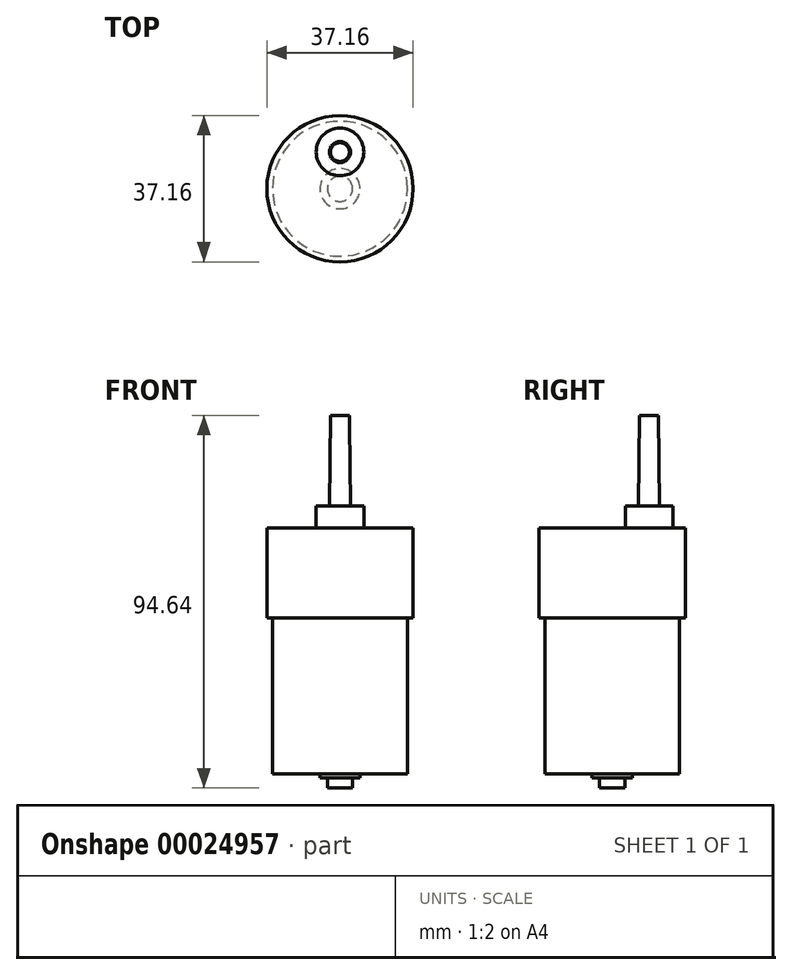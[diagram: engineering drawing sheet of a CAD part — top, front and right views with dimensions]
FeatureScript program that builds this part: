
annotation { "Feature Type Name" : "Feature", "Feature Type Description" : "" }
export const myFeature = defineFeature(function(context is Context, id is Id, definition is map)
    precondition{}
    {
        {
            var Q0;
            Q0=qCreatedBy(makeId("Top.planeOp"),FACE);
            var sketch = newSketch(context, id + "F0", { "sketchPlane" : qUnion([Q0])});
            skCircle(sketch, "E0", {"center": v(0, 0) * mm, "radius": 18.58 * mm});
            skPoint(sketch, "E1", {"position": v(-15.1, -10.83) * mm});
            skPoint(sketch, "E2", {"position": v(15.1, -10.83) * mm});
            skSolve(sketch);
        }
        {
            var Q0;
            Q0=makeQuery(id+"F0.imprint","IMPRINT",FACE,{"disambiguationData":[TD([[makeQuery(id+"F0.imprint","IMPRINT",EDGE,{"derivedFrom":sQuery(id+"F0.wireOp",EDGE,"E0")}),1.0]])]});
            extrude(context, id + "F1", {"entities" : qUnion([Q0]), "depth" : 22.8 * mm});
        }
        {
            var Q0;
            Q0=qCreatedBy(makeId("Top.planeOp"),FACE);
            var sketch = newSketch(context, id + "F2", { "sketchPlane" : qUnion([Q0])});
            skCircle(sketch, "E3", {"center": v(0, 9.35) * mm, "radius": 6.05 * mm});
            skSolve(sketch);
        }
        {
            var Q0;
            Q0 = qSketchRegion(id + "F2", true);
            extrude(context, id + "F3", {"entities" : qUnion([Q0]), "operationType" : NewBodyOperationType.ADD, "depth" : 28.45 * mm});
        }
        {
            var Q0;
            Q0=qCreatedBy(makeId("Top.planeOp"),FACE);
            var sketch = newSketch(context, id + "F4", { "sketchPlane" : qUnion([Q0])});
            skCircle(sketch, "E4", {"center": v(0, 9.32) * mm, "radius": 3.02 * mm});
            skSolve(sketch);
        }
        {
            var Q0;
            Q0 = qSketchRegion(id + "F4", true);
            extrude(context, id + "F5", {"entities" : qUnion([Q0]), "operationType" : NewBodyOperationType.ADD, "depth" : 51.46 * mm, "hasDraft" : true, "draftAngle" : 0.7 * degree, "draftPullDirection" : true});
        }
        {
            var Q0;
            Q0=qCreatedBy(makeId("Top.planeOp"),FACE);
            var sketch = newSketch(context, id + "F6", { "sketchPlane" : qUnion([Q0])});
            skCircle(sketch, "E5", {"center": v(0, 0) * mm, "radius": 17.14 * mm});
            skSolve(sketch);
        }
        {
            var Q0;
            Q0 = qSketchRegion(id + "F6", true);
            extrude(context, id + "F7", {"entities" : qUnion([Q0]), "operationType" : NewBodyOperationType.ADD, "oppositeDirection" : true, "depth" : 39.6 * mm});
        }
        {
            var Q0;
            Q0=qCreatedBy(makeId("Top.planeOp"),FACE);
            var sketch = newSketch(context, id + "F8", { "sketchPlane" : qUnion([Q0])});
            skCircle(sketch, "E6", {"center": v(0, 0) * mm, "radius": 5.1 * mm});
            skSolve(sketch);
        }
        {
            var Q0;
            Q0 = qSketchRegion(id + "F8", true);
            extrude(context, id + "F9", {"entities" : qUnion([Q0]), "operationType" : NewBodyOperationType.ADD, "oppositeDirection" : true, "depth" : 40.64 * mm});
        }
        {
            var Q0;
            Q0=qCreatedBy(makeId("Top.planeOp"),FACE);
            var sketch = newSketch(context, id + "F10", { "sketchPlane" : qUnion([Q0])});
            skCircle(sketch, "E7", {"center": v(0, 0) * mm, "radius": 3.21 * mm});
            skSolve(sketch);
        }
        {
            var Q0;
            Q0 = qSketchRegion(id + "F10", true);
            extrude(context, id + "F11", {"entities" : qUnion([Q0]), "operationType" : NewBodyOperationType.ADD, "oppositeDirection" : true, "depth" : 43.18 * mm});
        }
    });
